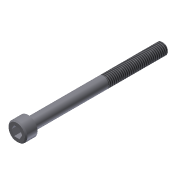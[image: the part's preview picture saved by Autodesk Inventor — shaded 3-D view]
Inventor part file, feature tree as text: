
AUTODESK INVENTOR PART (.ipt)
format: ipt  version: 2011 (Build 150239000, 239)  size: 97,280 bytes
history: native  units: in
note: dims shown in document units (in); Inventor stores cm internally (conversion verified against a paired STEP export)
features: extrude x3, sketch x3, chamfer x2, thread x1
ambient origin geometry x8: Origin, YZ Plane, XZ Plane, XY Plane, X Axis, Y Axis, Z Axis, Center Point
bodies: Solid1 (feature_tree)
feature tree (9):
  extrude  "Extrusion1"  Depth=0.19in TaperAngle=0.0deg
  extrude  "Extrusion2"  Depth=2.25in TaperAngle=0.0deg
  extrude  "Extrusion3"  Depth=0.125in TaperAngle=0.0deg
  thread  "Thread1"  [1 undecoded]
  chamfer  "Chamfer1"  Distance=0.02in Angle=45.0deg
  chamfer  "Chamfer2"  Distance=0.02in Angle=45.0deg
  sketch  "Sketch1"  dims[d0=0.312in d1=0.19in d2=0.0in]
  sketch  "Sketch2"  dims[d3=0.19in d4=2.25in d5=0.0in]
  sketch  "Sketch3"  dims[d6=0.1562in d7=0.125in d8=0.0in d9=1.0in d10=0.0in d11=0.02in d12=0.125in d13=45.0deg d14=0.02in d15=0.125in d16=45.0deg]
note: 1 required parameter value undecoded (feature->parameter linkage not recoverable at this tier; creation-order binding heuristic only, values carry confidence <= 0.55)
